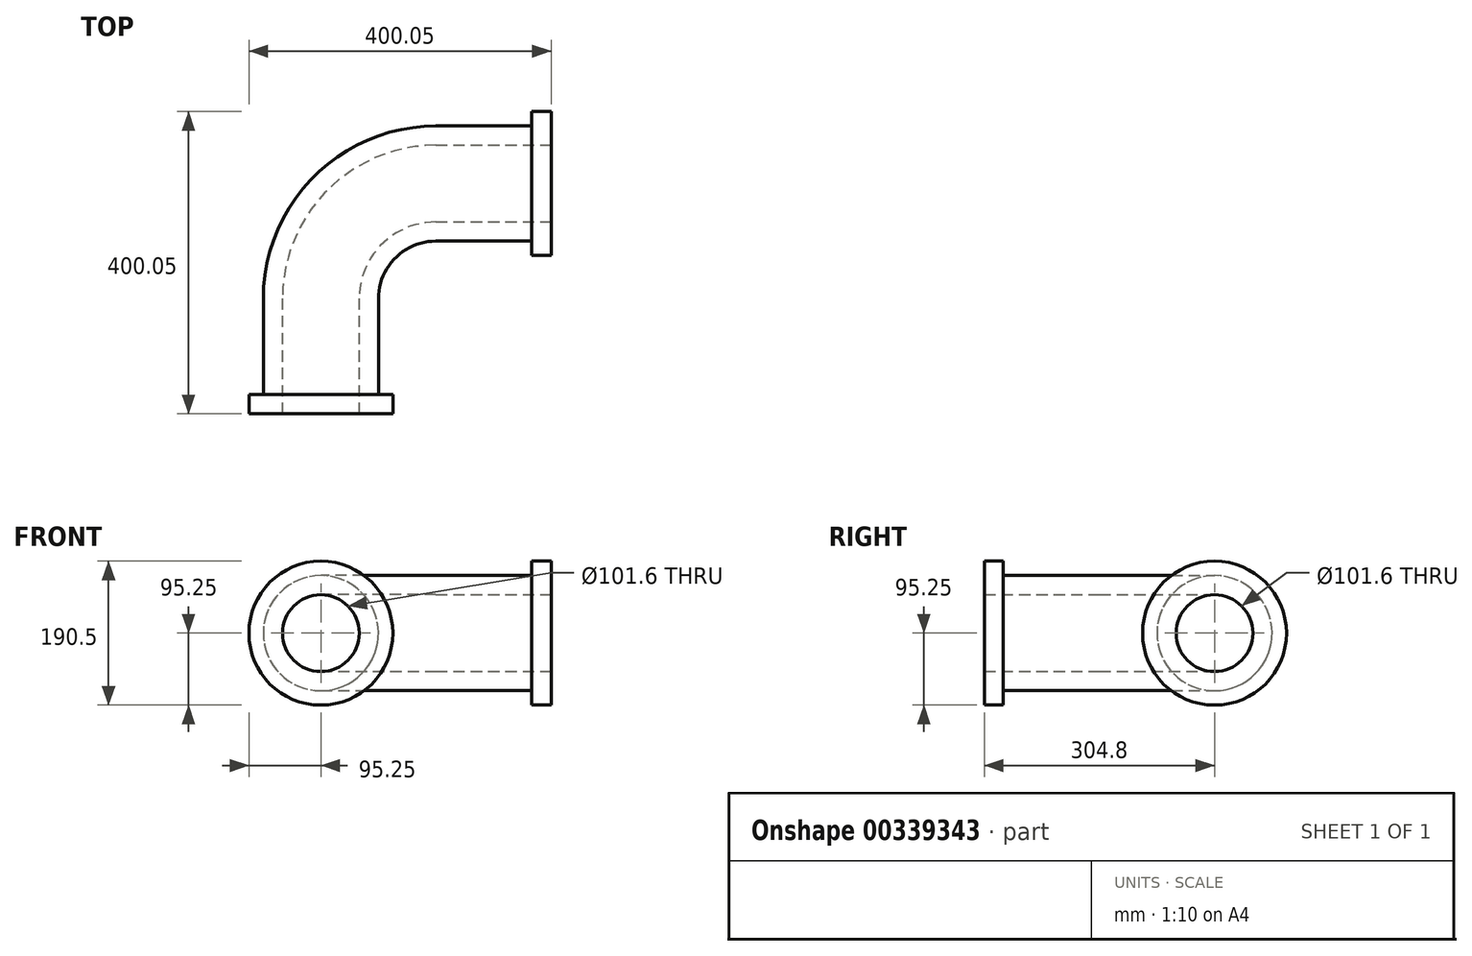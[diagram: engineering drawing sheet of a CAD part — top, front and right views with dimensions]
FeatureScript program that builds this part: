
annotation { "Feature Type Name" : "Feature", "Feature Type Description" : "" }
export const myFeature = defineFeature(function(context is Context, id is Id, definition is map)
    precondition{}
    {
        {
            var Q0;
            Q0=qCreatedBy(makeId("Front.planeOp"),FACE);
            var sketch = newSketch(context, id + "F0", { "sketchPlane" : qUnion([Q0])});
            skCircle(sketch, "E0", {"center": v(0, 0) * mm, "radius": 76.2 * mm});
            skCircle(sketch, "E1", {"center": v(0, 0) * mm, "radius": 95.25 * mm});
            skSolve(sketch);
        }
        {
            var Q0;
            Q0=qCreatedBy(makeId("Top.planeOp"),FACE);
            var sketch = newSketch(context, id + "F1", { "sketchPlane" : qUnion([Q0])});
            skLineSegment(sketch, "E2", {"start": v(0, 0) * mm, "end": v(0, 152.4) * mm});
            skLineSegment(sketch, "E3", {"start": v(152.4, 304.8) * mm, "end": v(304.8, 304.8) * mm});
            skPoint(sketch, "E4.visualSharp", {"position": v(0, 304.8) * mm});
            skArc(sketch, "E4.filletArc", {"start": v(152.4, 304.8) * mm, "mid": v(44.64, 260.16) * mm, "end": v(0, 152.4) * mm});
            skSolve(sketch);
        }
        {
            var Q0;
            Q0=makeQuery(id+"F0.imprint","IMPRINT",FACE,{"disambiguationData":[TD([[makeQuery(id+"F0.imprint","IMPRINT",EDGE,{"derivedFrom":sQuery(id+"F0.wireOp",EDGE,"E0")}),1.0]])]});
            var Q1;
            Q1=sQuery(id+"F1.wireOp",EDGE,"E2");
            var Q2;
            Q2=sQuery(id+"F1.wireOp",EDGE,"E4.filletArc");
            var Q3;
            Q3=sQuery(id+"F1.wireOp",EDGE,"E3");
            sweep(context, id + "F2", {"profiles" : qUnion([Q0]), "path" : qUnion([Q1, Q2, Q3])});
        }
        {
            var Q0;
            Q0=makeQuery(id+"F2.opSweep","CAP_FACE",FACE,{"disambiguationData":[OSD([sQuery(id+"F0.wireOp",EDGE,"E0"),sQuery(id+"F1.wireOp",VERTEX,"E2.start")])],"isStart":true});
            var Q1;
            Q1=makeQuery(id+"F2.opSweep","CAP_FACE",FACE,{"disambiguationData":[OSD([sQuery(id+"F0.wireOp",EDGE,"E0"),sQuery(id+"F1.wireOp",VERTEX,"E3.end")])],"isStart":false});
            var Q2;
            Q2=makeQuery(id+"F2.opSweep","SWEPT_BODY",BODY,{"disambiguationData":[OSD([sQuery(id+"F0.wireOp",EDGE,"E0"),sQuery(id+"F1.wireOp",EDGE,"E3")])]});
            shell(context, id + "F3", {"entities" : qUnion([Q0, Q1]), "parts" : qUnion([Q2]), "thickness" : 25.4 * mm});
        }
        {
            var Q0;
            Q0=makeQuery(id+"F0.imprint","IMPRINT",FACE,{"disambiguationData":[TD([[makeQuery(id+"F0.imprint","IMPRINT",EDGE,{"derivedFrom":sQuery(id+"F0.wireOp",EDGE,"E0")}),-1.0]])]});
            extrude(context, id + "F4", {"entities" : qUnion([Q0]), "operationType" : NewBodyOperationType.ADD, "depth" : -25.4 * mm, "offsetDistance" : 25.4 * mm});
        }
        {
            var Q0;
            Q0=sQuery(id+"F1.wireOp",EDGE,"E3");
            var Q1;
            Q1=sQuery(id+"F1.wireOp",VERTEX,"E3.end");
            cPlane(context, id + "F5", {"entities" : qUnion([Q0, Q1]), "cplaneType" : CPlaneType.LINE_POINT, "offset" : 25.4 * mm, "width" : 152.4 * mm, "height" : 152.4 * mm});
        }
        {
            var Q0;
            Q0=qCreatedBy(id+"F5.planeOp",FACE);
            var sketch = newSketch(context, id + "F6", { "sketchPlane" : qUnion([Q0])});
            skCircle(sketch, "E5", {"center": v(304.8, 0) * mm, "radius": 76.2 * mm});
            skCircle(sketch, "E6", {"center": v(304.8, 0) * mm, "radius": 95.25 * mm});
            skSolve(sketch);
        }
        {
            var Q0;
            Q0=makeQuery(id+"F6.imprint","IMPRINT",FACE,{"disambiguationData":[TD([[makeQuery(id+"F6.imprint","IMPRINT",EDGE,{"derivedFrom":sQuery(id+"F6.wireOp",EDGE,"E5")}),-1.0]])]});
            extrude(context, id + "F7", {"entities" : qUnion([Q0]), "operationType" : NewBodyOperationType.ADD, "depth" : -25.4 * mm, "offsetDistance" : 25.4 * mm});
        }
    });
